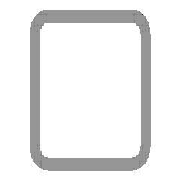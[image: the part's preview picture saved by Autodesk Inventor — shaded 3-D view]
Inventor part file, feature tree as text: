
AUTODESK INVENTOR PART (.ipt)
format: ipt  version: 2025 (Build 290162010, 162A)  size: 132,608 bytes
history: native  units: mm (DEFAULTED — no unit token found)
features: other x4, sketch x1, plane x1
ambient origin geometry x8: Origin, YZ Plane, XZ Plane, XY Plane, X Axis, Y Axis, Z Axis, Center Point
bodies: Solid1 (feature_tree), Body (feature_tree)
feature tree (6):
  parser-record x1  (decoder bookkeeping rows leaked as tree rows — omitted from the tree; the rows remain in map.json)
  other  "Driven Length"
  other  "Start Plane"
  other  "End Plane"
  sketch  "Sketch3"  dims[d3=2450.0mm d4=0.0mm d7=6.0mm d9=80.0mm d11=80.0mm d12=3.0mm d13=-0.0mm d14=2450.0mm d15=40.0mm d16=40.0mm d17=90.0deg d18=2450.0mm]
  plane  "Work Plane3"
